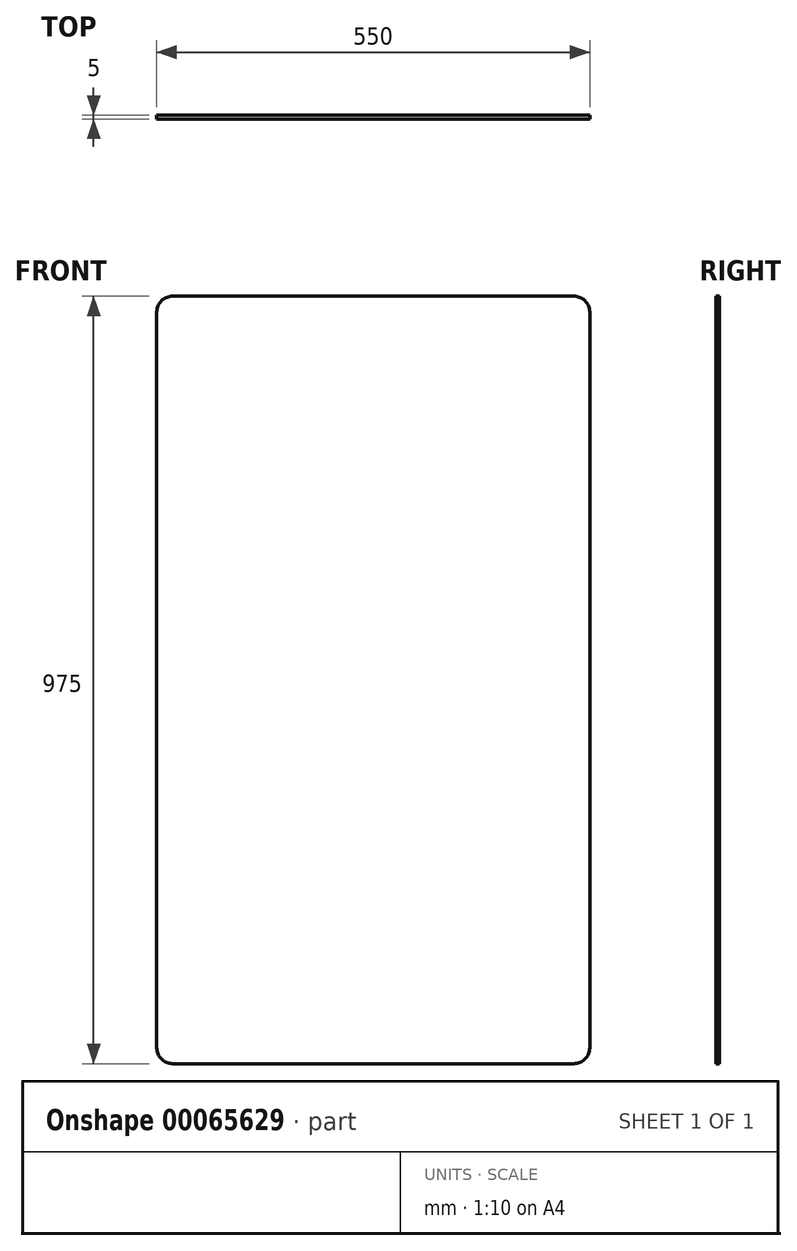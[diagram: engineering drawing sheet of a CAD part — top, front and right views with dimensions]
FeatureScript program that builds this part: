
annotation { "Feature Type Name" : "Feature", "Feature Type Description" : "" }
export const myFeature = defineFeature(function(context is Context, id is Id, definition is map)
    precondition{}
    {
        {
            var Q0;
            Q0=qCreatedBy(makeId("Front.planeOp"),FACE);
            var sketch = newSketch(context, id + "F0", { "sketchPlane" : qUnion([Q0])});
            skLineSegment(sketch, "E0.rect.bottom", {"start": v(-255, 482.5) * mm, "end": v(255, 482.5) * mm});
            skLineSegment(sketch, "E0.rect.top", {"start": v(-255, -482.5) * mm, "end": v(255, -482.5) * mm});
            skLineSegment(sketch, "E0.rect.left", {"start": v(-270, 467.5) * mm, "end": v(-270, -467.5) * mm});
            skLineSegment(sketch, "E0.rect.right", {"start": v(270, 467.5) * mm, "end": v(270, -467.5) * mm});
            skPoint(sketch, "E0.rect.middle", {"position": v(0, 0) * mm});
            skPoint(sketch, "E1.visualSharp", {"position": v(270, 482.5) * mm});
            skArc(sketch, "E1.filletArc", {"start": v(270, 467.5) * mm, "mid": v(265.6, 478.1) * mm, "end": v(255, 482.5) * mm});
            skPoint(sketch, "E2.visualSharp", {"position": v(-270, 482.5) * mm});
            skArc(sketch, "E2.filletArc", {"start": v(-255, 482.5) * mm, "mid": v(-265.6, 478.1) * mm, "end": v(-270, 467.5) * mm});
            skPoint(sketch, "E3.visualSharp", {"position": v(-270, -482.5) * mm});
            skArc(sketch, "E3.filletArc", {"start": v(-270, -467.5) * mm, "mid": v(-265.6, -478.1) * mm, "end": v(-255, -482.5) * mm});
            skPoint(sketch, "E4.visualSharp", {"position": v(270, -482.5) * mm});
            skArc(sketch, "E4.filletArc", {"start": v(255, -482.5) * mm, "mid": v(265.6, -478.1) * mm, "end": v(270, -467.5) * mm});
            skArc(sketch, "E5.0", {"start": v(-255, 487.5) * mm, "mid": v(-269.14, 481.64) * mm, "end": v(-275, 467.5) * mm});
            skLineSegment(sketch, "E5.1", {"start": v(-275, 467.5) * mm, "end": v(-275, -467.5) * mm});
            skLineSegment(sketch, "E5.2", {"start": v(-255, 487.5) * mm, "end": v(255, 487.5) * mm});
            skArc(sketch, "E5.3", {"start": v(-275, -467.5) * mm, "mid": v(-269.14, -481.64) * mm, "end": v(-255, -487.5) * mm});
            skArc(sketch, "E5.4", {"start": v(275, 467.5) * mm, "mid": v(269.14, 481.64) * mm, "end": v(255, 487.5) * mm});
            skLineSegment(sketch, "E5.5", {"start": v(275, 467.5) * mm, "end": v(275, -467.5) * mm});
            skArc(sketch, "E5.6", {"start": v(255, -487.5) * mm, "mid": v(269.14, -481.64) * mm, "end": v(275, -467.5) * mm});
            skLineSegment(sketch, "E5.7", {"start": v(-255, -487.5) * mm, "end": v(255, -487.5) * mm});
            skSolve(sketch);
        }
        {
            var Q0;
            Q0 = qSketchRegion(id + "F0", true);
            var Q1;
            Q1=makeQuery(id+"F0.imprint","IMPRINT",FACE,{"disambiguationData":[TD([[makeQuery(id+"F0.imprint","IMPRINT",EDGE,{"derivedFrom":sQuery(id+"F0.wireOp",EDGE,"E0.rect.bottom")}),-1.0]])]});
            extrude(context, id + "F1", {"entities" : qUnion([Q0, Q1]), "depth" : 5 * mm});
        }
    });
